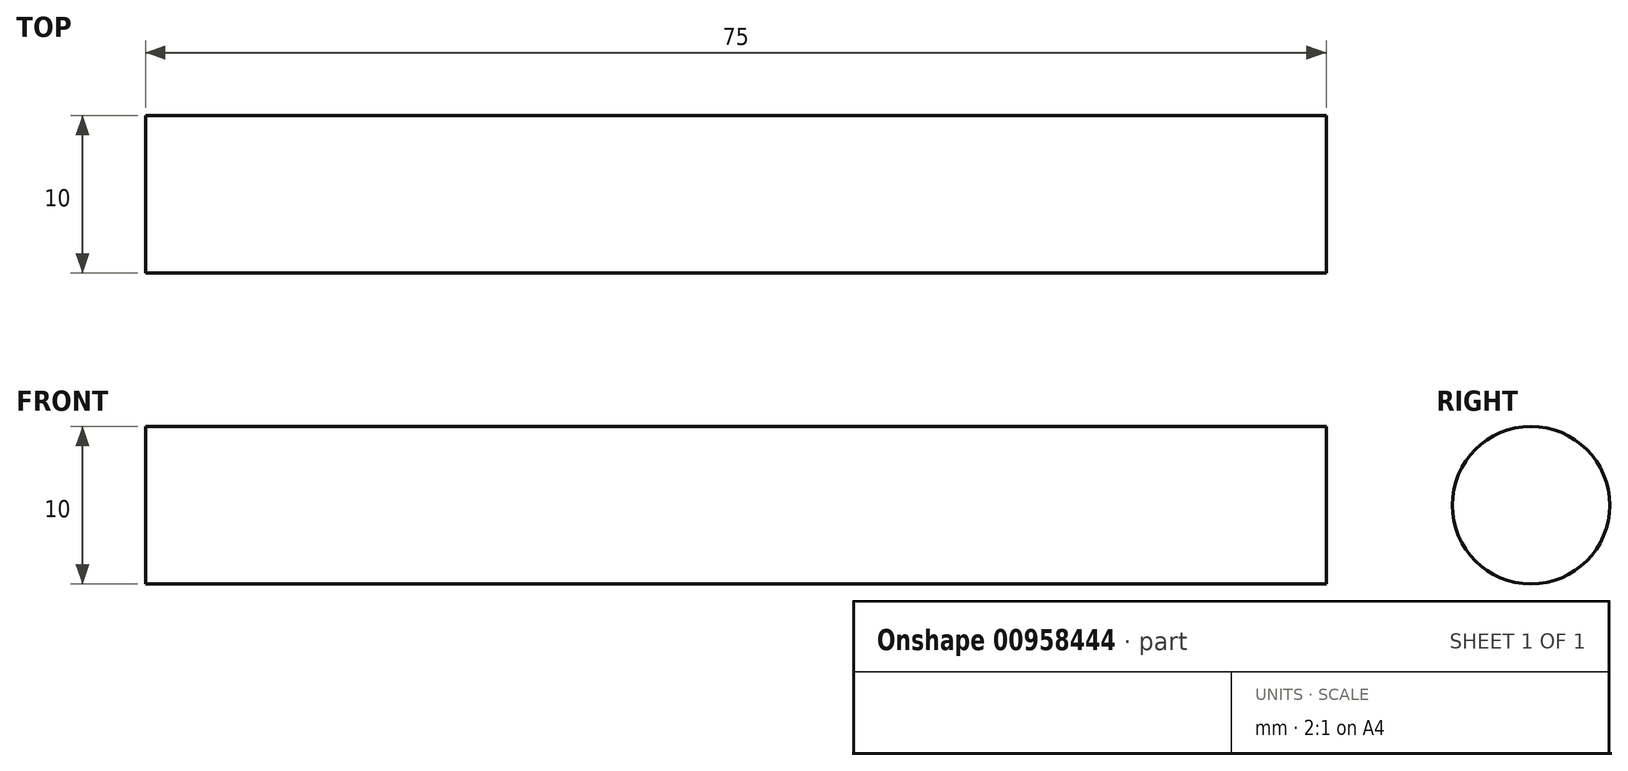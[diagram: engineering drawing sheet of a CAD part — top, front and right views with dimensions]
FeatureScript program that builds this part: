
annotation { "Feature Type Name" : "Feature", "Feature Type Description" : "" }
export const myFeature = defineFeature(function(context is Context, id is Id, definition is map)
    precondition{}
    {
        {
            var Q0;
            Q0=qCreatedBy(makeId("Right.planeOp"),FACE);
            var sketch = newSketch(context, id + "F0", { "sketchPlane" : qUnion([Q0])});
            skCircle(sketch, "E0", {"center": v(0, 0) * mm, "radius": 5 * mm});
            skSolve(sketch);
        }
        {
            var Q0;
            Q0=makeQuery(id+"F0.imprint","IMPRINT",FACE,{"disambiguationData":[TD([[makeQuery(id+"F0.imprint","IMPRINT",EDGE,{"derivedFrom":sQuery(id+"F0.wireOp",EDGE,"E0")}),1.0]])]});
            extrude(context, id + "F1", {"entities" : qUnion([Q0]), "depth" : 75 * mm, "offsetDistance" : 25 * mm});
        }
    });
